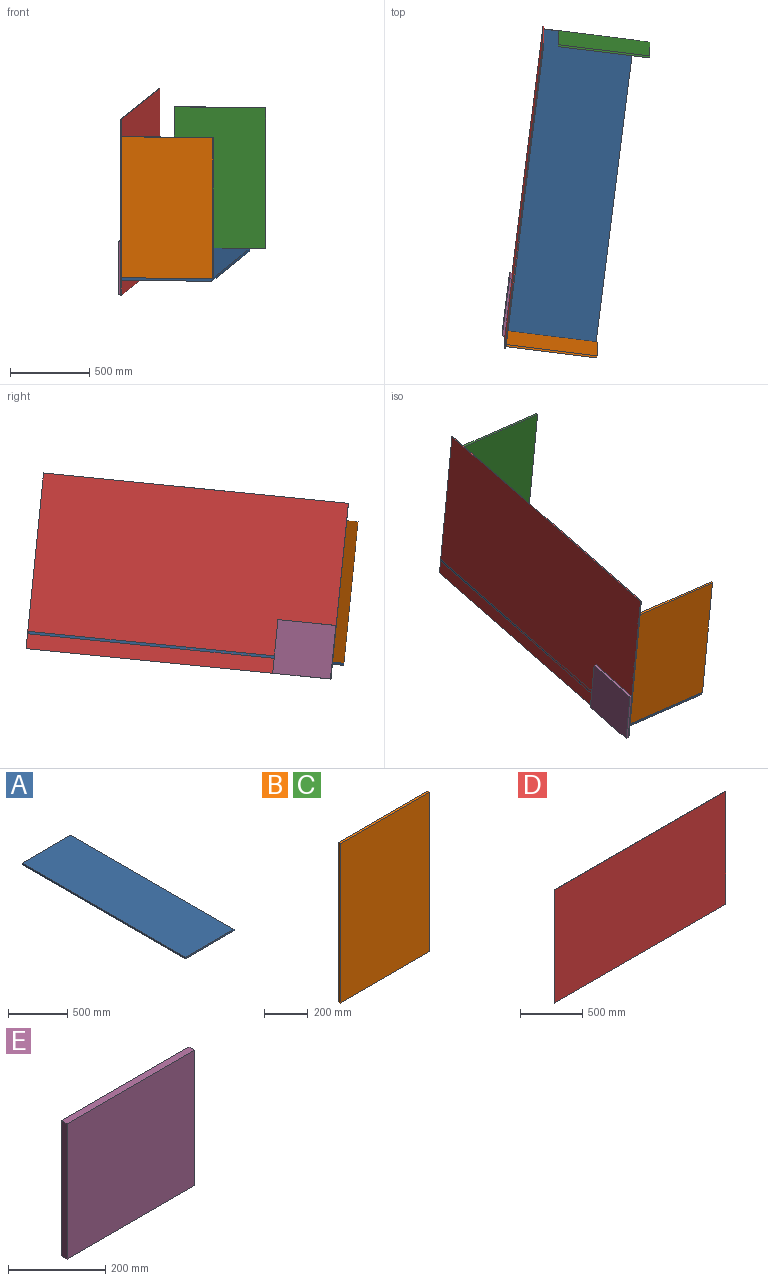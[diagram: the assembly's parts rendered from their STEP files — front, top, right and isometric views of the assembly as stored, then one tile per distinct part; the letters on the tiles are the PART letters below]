
ASSEMBLY  parts=5 mates=10
PART A: 6 faces, bbox 580x1943.1x15.9 mm
  f0: plane 1943.1x15.88mm, normal (1,0,0), area 30846.7mm2, adj f1,f3,f4,f5
  f1: plane 580x15.88mm, normal (0,1,0), area 9207.5mm2, adj f0,f2,f4,f5
  f2: plane 1943.1x15.88mm, normal (-1,0,0), area 30846.7mm2, adj f1,f3,f4,f5
  f3: plane 580x15.88mm, normal (0,-1,0), area 9207.5mm2, adj f0,f2,f4,f5
  f4: plane 1943.1x580mm, normal (0,0,1), area 1126998mm2, adj f0,f1,f2,f3
  f5: plane 1943.1x580mm, normal (0,0,-1), area 1126998mm2, adj f0,f1,f2,f3
PART B: 6 faces, bbox 580x12.7x895 mm
  f0: plane 895x12.7mm, normal (1,0,0), area 11366.5mm2, adj f1,f3,f4,f5
  f1: plane 580x12.7mm, normal (0,0,1), area 7366mm2, adj f0,f2,f4,f5
  f2: plane 895x12.7mm, normal (-1,0,0), area 11366.5mm2, adj f1,f3,f4,f5
  f3: plane 580x12.7mm, normal (0,0,-1), area 7366mm2, adj f0,f2,f4,f5
  f4: plane 895x580mm, normal (0,-1,0), area 519100mm2, adj f0,f1,f2,f3
  f5: plane 895x580mm, normal (0,1,0), area 519100mm2, adj f0,f1,f2,f3
PART C: same geometry as B
PART D: 6 faces, bbox 1950x6.4x1115 mm
  f0: plane 1950x6.35mm, normal (0,0,1), area 12382.5mm2, adj f1,f3,f4,f5
  f1: plane 1115x6.35mm, normal (-1,0,0), area 7080.2mm2, adj f0,f2,f4,f5
  f2: plane 1950x6.35mm, normal (0,0,-1), area 12382.5mm2, adj f1,f3,f4,f5
  f3: plane 1115x6.35mm, normal (1,0,0), area 7080.2mm2, adj f0,f2,f4,f5
  f4: plane 1950x1115mm, normal (0,-1,0), area 2174250mm2, adj f0,f1,f2,f3
  f5: plane 1950x1115mm, normal (0,1,0), area 2174250mm2, adj f0,f1,f2,f3
PART E: 6 faces, bbox 370x15.9x340 mm
  f0: plane 340x15.88mm, normal (1,0,0), area 5397.5mm2, adj f1,f3,f4,f5
  f1: plane 370x15.88mm, normal (0,0,1), area 5873.7mm2, adj f0,f2,f4,f5
  f2: plane 340x15.88mm, normal (-1,0,0), area 5397.5mm2, adj f1,f3,f4,f5
  f3: plane 370x15.88mm, normal (0,0,-1), area 5873.7mm2, adj f0,f2,f4,f5
  f4: plane 370x340mm, normal (0,-1,0), area 125800mm2, adj f0,f1,f2,f3
  f5: plane 370x340mm, normal (0,1,0), area 125800mm2, adj f0,f1,f2,f3
PLACE A rot(axis=(0.63,0.04,-0.78),9.1deg) t=(194.94,1863.87,126.94)mm
PLACE B rot(axis=(0.63,0.04,-0.78),9.1deg) t=(82.8,870.29,493.5)mm
PLACE C rot(axis=(0.63,0.04,-0.78),9.1deg) t=(414.88,2764.84,682.5)mm
PLACE D rot(axis=(0.06,-0.05,1),83.1deg) t=(-92.41,1856.93,591.92)mm
PLACE E rot(axis=(-0.75,-0.66,-0.03),175.7deg) t=(-190,1115.31,128.52)mm
MATE planar E.f5 <-> D.f5  axis (0.99,-0.12,-0.01) through (-190,1115.31,128.52)mm
MATE planar E.f1 <-> D.f2  axis (0,0.1,-1) through (-197.87,1133.16,-40.54)mm
MATE planar B.f3 <-> A.f4  axis (0,0.1,-1) through (82.02,908.44,47.59)mm
MATE planar D.f4 <-> B.f2  axis (0.99,-0.12,-0.01) through (-86.11,1856.15,591.85)mm
MATE planar E.f2 <-> B.f4  axis (-0.12,-0.99,-0.1) through (-220.73,933.61,110.39)mm
MATE planar D.f1 <-> B.f4  axis (-0.12,-0.99,-0.1) through (-209.7,893.78,495.84)mm
MATE planar C.f3 <-> A.f4  axis (0,0.1,-1) through (414.09,2803,236.58)mm
MATE planar C.f5 <-> A.f1  axis (0.12,0.99,0.1) through (414.88,2764.84,682.5)mm
MATE planar B.f4 <-> A.f3  axis (-0.12,-0.99,-0.1) through (81.23,857.75,492.25)mm
MATE planar D.f5 <-> A.f2  axis (-0.99,0.12,0.01) through (-92.41,1856.93,591.92)mm
